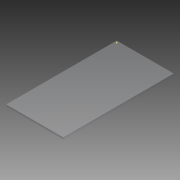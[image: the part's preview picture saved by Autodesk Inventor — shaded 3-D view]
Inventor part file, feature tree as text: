
AUTODESK INVENTOR PART (.ipt)
format: ipt  version: 2015 (Build 190159000, 159)  size: 83,968 bytes
history: native  units: in
note: dims shown in document units (in); Inventor stores cm internally (conversion verified against a paired STEP export)
features: sketch x2, extrude x1
ambient origin geometry x8: Origin, YZ Plane, XZ Plane, XY Plane, X Axis, Y Axis, Z Axis, Center Point
bodies: Solid1 (feature_tree)
feature tree (3):
  sketch  "Sketch1"  dims[d0=8.622in d1=0.2756in]
  extrude  "Extrusion1"  Depth=0.2756in
  sketch  "Sketch2"  dims[d2=16.6929in d3=0.0in]
